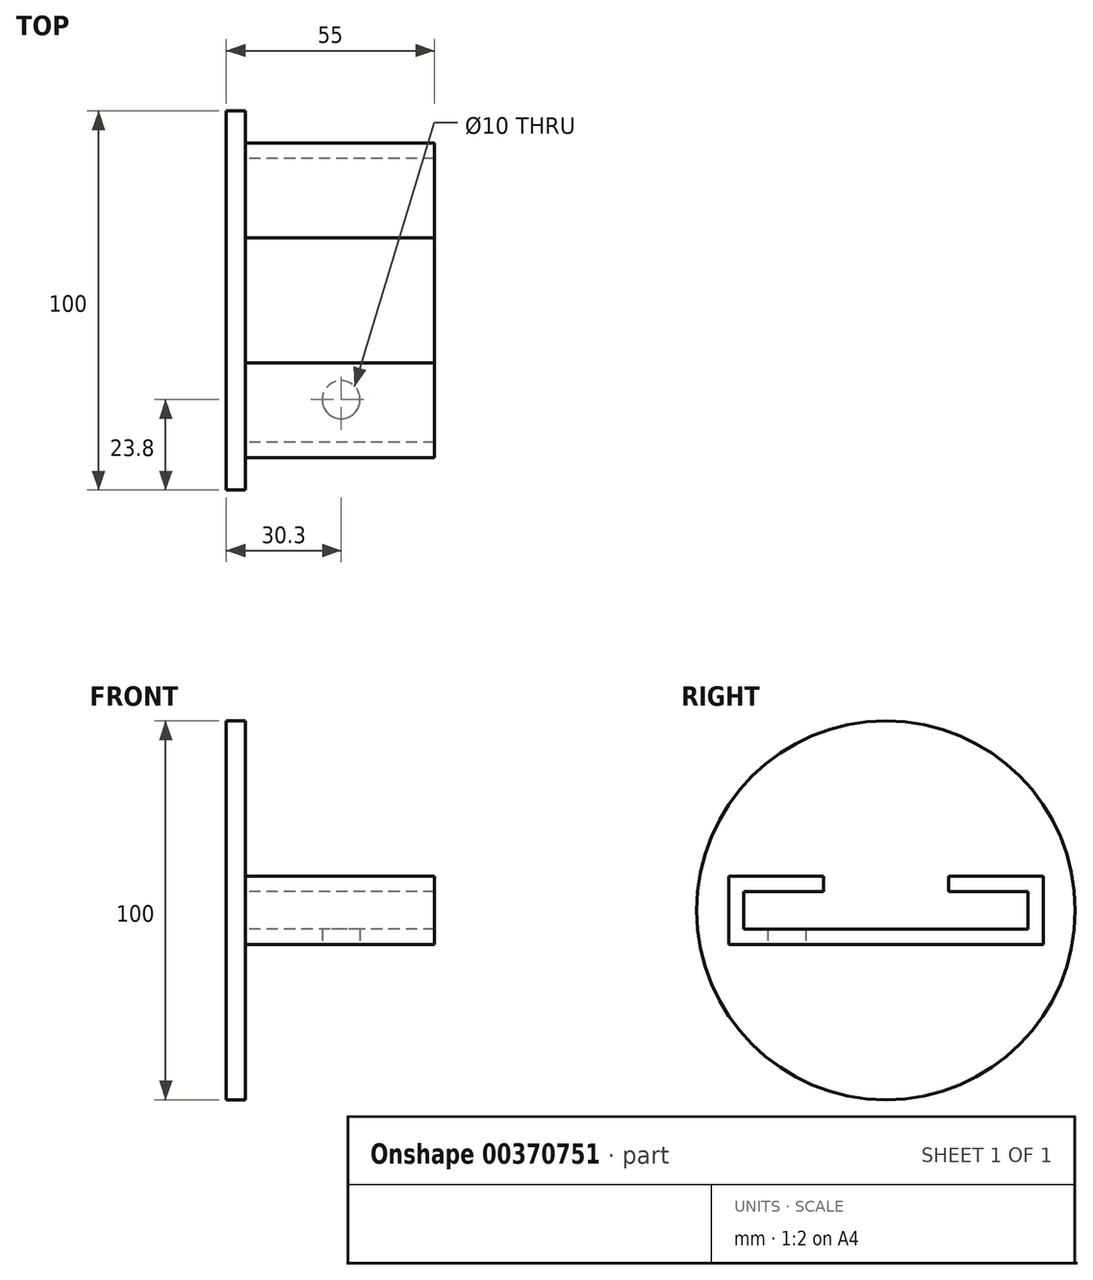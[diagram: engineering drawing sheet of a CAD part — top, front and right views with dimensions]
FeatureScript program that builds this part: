
annotation { "Feature Type Name" : "Feature", "Feature Type Description" : "" }
export const myFeature = defineFeature(function(context is Context, id is Id, definition is map)
    precondition{}
    {
        {
            var Q0;
            Q0=qCreatedBy(makeId("Right.planeOp"),FACE);
            var sketch = newSketch(context, id + "F0", { "sketchPlane" : qUnion([Q0])});
            skCircle(sketch, "E0", {"center": v(0, 0) * mm, "radius": 50 * mm});
            skSolve(sketch);
        }
        {
            var Q0;
            Q0=makeQuery(id+"F0.imprint","IMPRINT",FACE,{"disambiguationData":[TD([[makeQuery(id+"F0.imprint","IMPRINT",EDGE,{"derivedFrom":sQuery(id+"F0.wireOp",EDGE,"E0")}),1.0]])]});
            var Q1;
            Q1=sQuery(id+"F0.wireOp",EDGE,"E0");
            extrude(context, id + "F1", {"entities" : qUnion([Q0]), "surfaceEntities" : qUnion([Q1]), "oppositeDirection" : true, "depth" : 5 * mm});
        }
        {
            var Q0;
            Q0=qCreatedBy(makeId("Right.planeOp"),FACE);
            var sketch = newSketch(context, id + "F2", { "sketchPlane" : qUnion([Q0])});
            skLineSegment(sketch, "E1", {"start": v(-41.5, -9) * mm, "end": v(41.5, -9) * mm});
            skLineSegment(sketch, "E2", {"start": v(-41.5, -9) * mm, "end": v(-41.5, 9) * mm});
            skLineSegment(sketch, "E3", {"start": v(41.5, -9) * mm, "end": v(41.5, 9) * mm});
            skLineSegment(sketch, "E4", {"start": v(-41.5, 9) * mm, "end": v(-16.5, 9) * mm});
            skLineSegment(sketch, "E5", {"start": v(-16.5, 9) * mm, "end": v(-16.5, 5) * mm});
            skLineSegment(sketch, "E6", {"start": v(-16.5, 5) * mm, "end": v(-37.5, 5) * mm});
            skLineSegment(sketch, "E7", {"start": v(-37.5, 5) * mm, "end": v(-37.5, -5) * mm});
            skLineSegment(sketch, "E8", {"start": v(-37.5, -5) * mm, "end": v(37.5, -5) * mm});
            skLineSegment(sketch, "E9", {"start": v(37.5, -5) * mm, "end": v(37.5, 5) * mm});
            skLineSegment(sketch, "E10", {"start": v(37.5, 5) * mm, "end": v(16.5, 5) * mm});
            skLineSegment(sketch, "E11", {"start": v(16.5, 5) * mm, "end": v(16.5, 9) * mm});
            skLineSegment(sketch, "E12", {"start": v(16.5, 9) * mm, "end": v(41.5, 9) * mm});
            skSolve(sketch);
        }
        {
            var Q0;
            Q0=makeQuery(id+"F2.imprint","IMPRINT",FACE,{"disambiguationData":[TD([[makeQuery(id+"F2.imprint","IMPRINT",EDGE,{"derivedFrom":sQuery(id+"F2.wireOp",EDGE,"E1")}),1.0]])]});
            extrude(context, id + "F3", {"entities" : qUnion([Q0]), "operationType" : NewBodyOperationType.ADD, "depth" : 50 * mm});
        }
        {
            var Q0;
            Q0=makeQuery(id+"F3.opExtrude","SWEPT_FACE",FACE,{"disambiguationData":[OSD([sQuery(id+"F2.wireOp",EDGE,"E1")])]});
            var sketch = newSketch(context, id + "F4", { "sketchPlane" : qUnion([Q0])});
            skCircle(sketch, "E13", {"center": v(25.3, 26.2) * mm, "radius": 5 * mm});
            skSolve(sketch);
        }
        {
            var Q0;
            Q0=makeQuery(id+"F4.imprint","IMPRINT",FACE,{"disambiguationData":[TD([[makeQuery(id+"F4.imprint","IMPRINT",EDGE,{"derivedFrom":sQuery(id+"F4.wireOp",EDGE,"E13")}),1.0]])]});
            extrude(context, id + "F5", {"entities" : qUnion([Q0]), "operationType" : NewBodyOperationType.REMOVE, "endBound" : BoundingType.UP_TO_NEXT, "oppositeDirection" : true, "depth" : 10 * mm});
        }
    });
